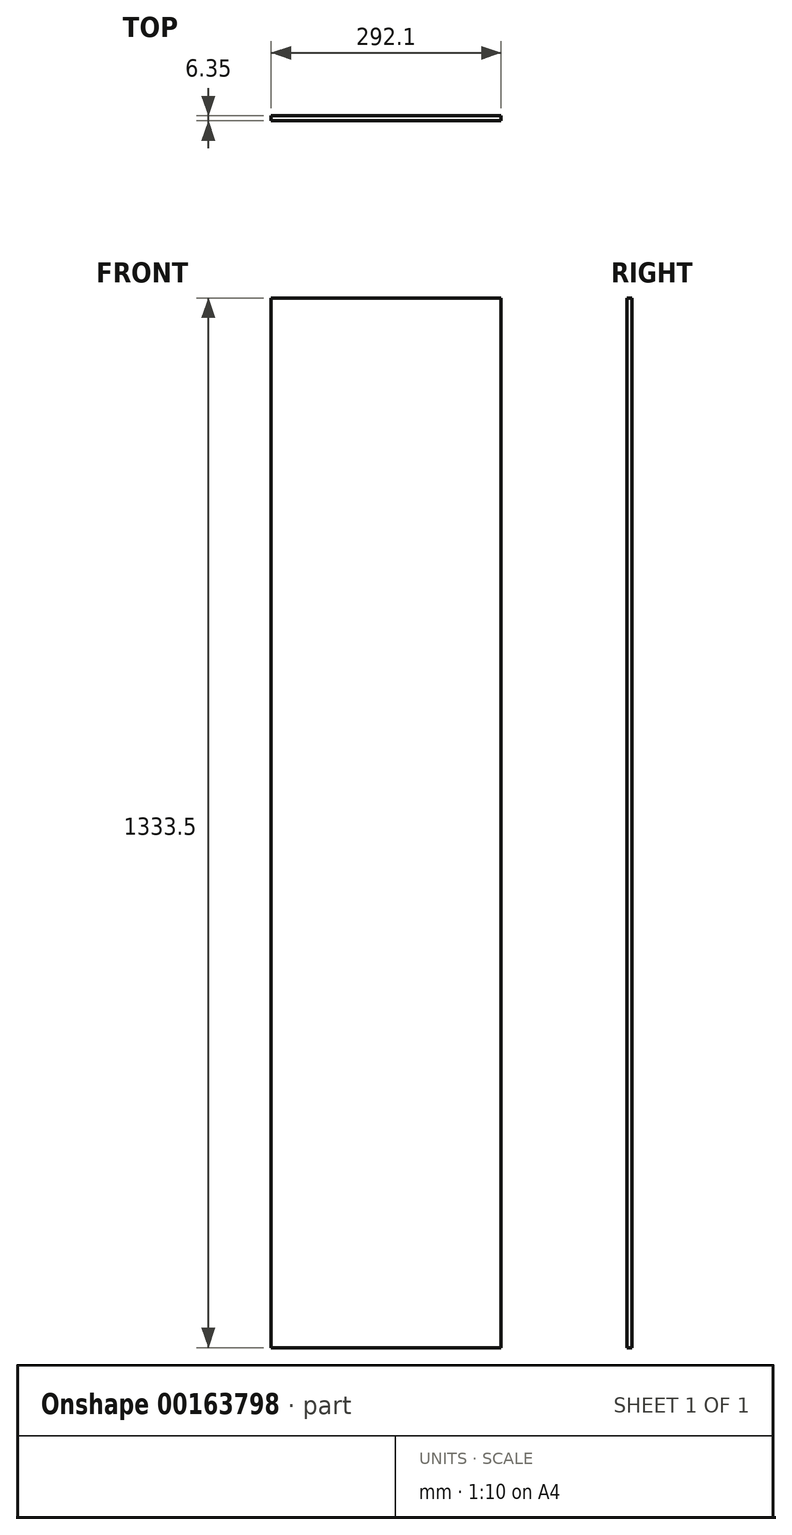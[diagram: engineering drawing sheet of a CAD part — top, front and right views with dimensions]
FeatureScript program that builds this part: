
annotation { "Feature Type Name" : "Feature", "Feature Type Description" : "" }
export const myFeature = defineFeature(function(context is Context, id is Id, definition is map)
    precondition{}
    {
        {
            var Q0;
            Q0=qCreatedBy(makeId("Front.planeOp"),FACE);
            var sketch = newSketch(context, id + "F0", { "sketchPlane" : qUnion([Q0])});
            skLineSegment(sketch, "E0.bottom", {"start": v(-146.05, -666.75) * mm, "end": v(146.05, -666.75) * mm});
            skLineSegment(sketch, "E0.top", {"start": v(-146.05, 666.75) * mm, "end": v(146.05, 666.75) * mm});
            skLineSegment(sketch, "E0.left", {"start": v(-146.05, -666.75) * mm, "end": v(-146.05, 666.75) * mm});
            skLineSegment(sketch, "E0.right", {"start": v(146.05, -666.75) * mm, "end": v(146.05, 666.75) * mm});
            skPoint(sketch, "E0.middle", {"position": v(0, 0) * mm});
            skSolve(sketch);
        }
        {
            var Q0;
            Q0=qSketchRegion(id+"F0",true);
            extrude(context, id + "F1", {"entities" : qUnion([Q0]), "depth" : 6.35 * mm});
        }
    });
